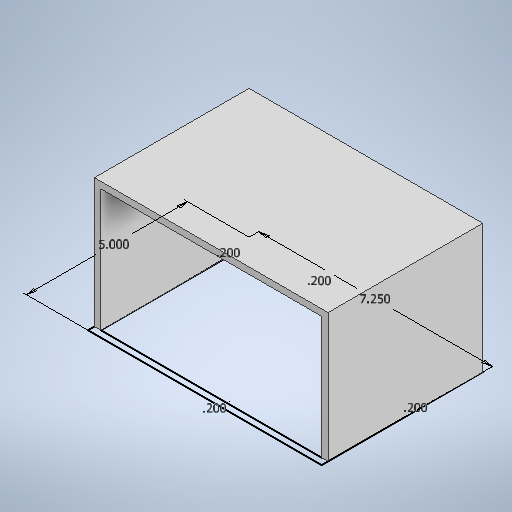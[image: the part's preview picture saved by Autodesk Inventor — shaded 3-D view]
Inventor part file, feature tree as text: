
AUTODESK INVENTOR PART (.ipt)
format: ipt  version: 2025.1 (Build 291241020, 241B)  size: 224,768 bytes
history: native  units: in
note: dims shown in document units (in); Inventor stores cm internally (conversion verified against a paired STEP export)
features: extrude x3, sketch x2
ambient origin geometry x8: Origin, YZ Plane, XZ Plane, XY Plane, X Axis, Y Axis, Z Axis, Center Point
bodies: Solid1 (feature_tree)
feature tree (5):
  sketch  "Sketch2"  dims[d0=7.25in d1=5.0in]
  extrude  "Extrusion1"  Depth=5.0in
  extrude  "Extrusion2"  Depth=0.2in
  extrude  "Extrusion3"  Depth=0.2in
  sketch  "Sketch3"  dims[d2=0.2in d3=0.2in d4=0.2in d5=0.2in d6=4.0in d7=0.0in d8=3.8in d9=0.0in d10=7.25in d11=4.0in d12=3.8in d13=0.0in]
